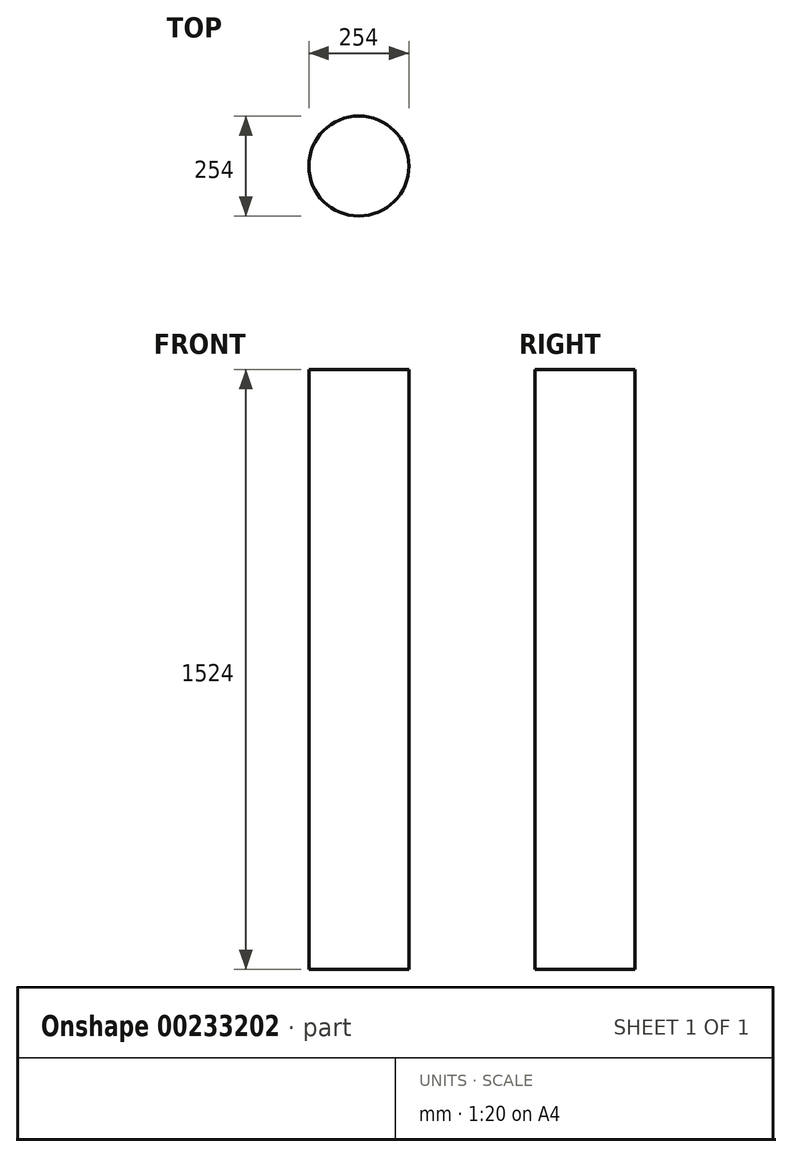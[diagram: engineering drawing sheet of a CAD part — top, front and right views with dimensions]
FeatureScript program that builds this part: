
annotation { "Feature Type Name" : "Feature", "Feature Type Description" : "" }
export const myFeature = defineFeature(function(context is Context, id is Id, definition is map)
    precondition{}
    {
        {
            var Q0;
            Q0=qCreatedBy(makeId("Top.planeOp"),FACE);
            var sketch = newSketch(context, id + "F0", { "sketchPlane" : qUnion([Q0])});
            skCircle(sketch, "E0", {"center": v(0, 0) * mm, "radius": 127 * mm});
            skSolve(sketch);
        }
        {
            var Q0;
            Q0 = qSketchRegion(id + "F0", true);
            extrude(context, id + "F1", {"entities" : qUnion([Q0]), "depth" : 1524 * mm});
        }
    });
